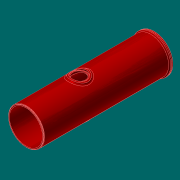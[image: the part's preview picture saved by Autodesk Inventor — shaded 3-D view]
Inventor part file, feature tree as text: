
AUTODESK INVENTOR PART (.ipt)
format: ipt  version: 2017.3 (Build 213257000, 257)  size: 373,760 bytes
history: native  units: in
note: dims shown in document units (in); Inventor stores cm internally (conversion verified against a paired STEP export)
features: extrude x10, sketch x8, fillet x3, chamfer x2, plane x2, pattern_circular x1, other x1, projected_geometry x1
ambient origin geometry x8: Origin, YZ Plane, XZ Plane, XY Plane, X Axis, Y Axis, Z Axis, Center Point
bodies: Solid1 (feature_tree)
feature tree (28):
  extrude  "Extrusion1"  Depth=31.0in
  extrude  "Extrusion2"  Depth=32.75in
  extrude  "Extrusion3"  Depth=32.48in
  chamfer  "Chamfer1"  Distance=1.0in
  extrude  "Extrusion4"  Depth=0.125in TaperAngle=45.0deg
  chamfer  "Chamfer2"  Distance=0.5in
  fillet  "Fillet1"  Radius=0.0312in
  extrude  "Extrusion5"  Depth=17.3228in
  plane  "Work Plane3"
  sketch  "Sketch7"  dims[d16=0.0312in d17=0.125in d18=45.0deg d19=0.0312in]
  extrude  "Extrusion9"  Depth=0.0312in
  extrude  "Extrusion11"  Depth=0.0312in TaperAngle=0.0deg
  sketch  "Sketch9"  dims[d22=11.1417in d23=47.0866in d24=0.5in d25=0.0in d39=15.1417in d40=1.0in d41=0.0in d42=12.75in d43=32.75in d44=110.0in d45=0.0in d48=2.0in d50=0.7874in d51=360.0deg d53=3.0in d54=1.0in d55=0.0in d56=1.0in d57=0.0in d58=0.0312in d59=0.5in d60=0.0in]
  extrude  "Extrusion12"  Depth=0.0312in
  extrude  "Extrusion13"  Depth=0.0312in TaperAngle=0.0deg
  fillet  "Fillet3"  Radius=12.75in
  fillet  "Fillet5"  Radius=32.75in
  pattern_circular  "Circular Pattern2"  [2 undecoded]
  sketch  "Sketch1"  dims[d0=28.5in d1=31.0in]
  sketch  "Sketch2"  dims[d2=110.0in d3=0.0in d4=32.75in]
  sketch  "Sketch3"  dims[d5=2.0in d6=0.0in d7=32.48in d8=1.0in d9=0.0in]
  sketch  "Sketch4"  dims[d10=0.875in d11=0.125in d12=45.0deg]
  sketch  "Sketch5"  dims[d13=29.98in d14=0.5in d15=0.0in]
  plane  "Work Plane2"
  sketch  "Sketch8"  dims[d20=2.5984in d21=17.3228in]
  other  "Srf1"
  projected_geometry  "Projected Loop1"
  extrude  "ExtrusionSrf1"  TaperAngle=0.0deg  [1 undecoded]
note: 3 required parameter values undecoded (feature->parameter linkage not recoverable at this tier; creation-order binding heuristic only, values carry confidence <= 0.55)
